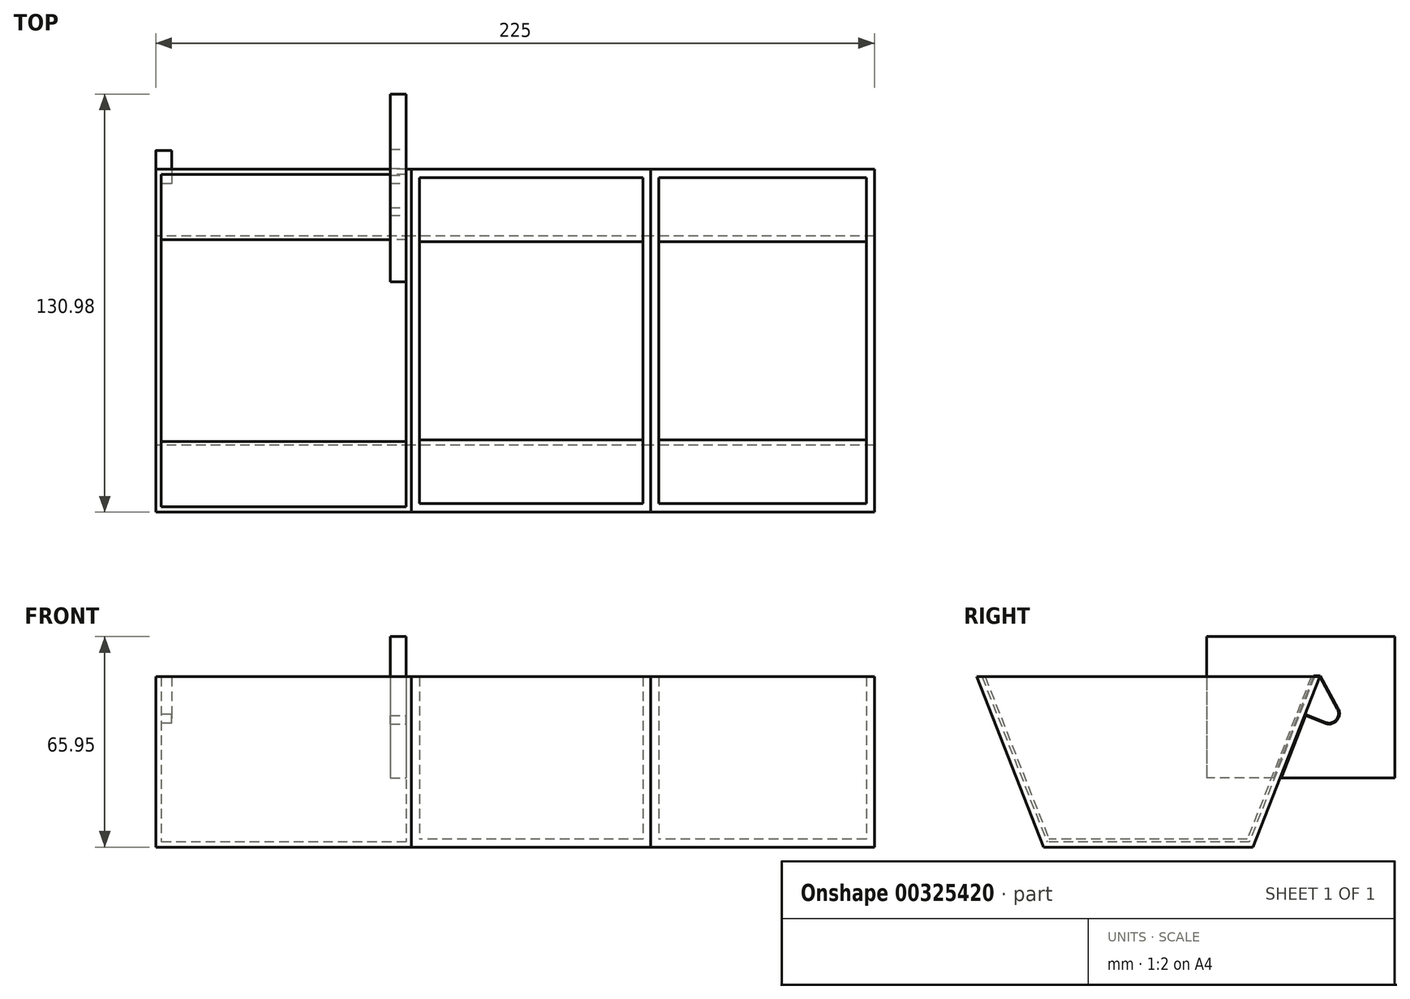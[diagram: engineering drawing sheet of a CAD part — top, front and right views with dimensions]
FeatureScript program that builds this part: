
annotation { "Feature Type Name" : "Feature", "Feature Type Description" : "" }
export const myFeature = defineFeature(function(context is Context, id is Id, definition is map)
    precondition{}
    {
        {
            var Q0;
            Q0=qCreatedBy(makeId("Right.planeOp"),FACE);
            var sketch = newSketch(context, id + "F0", { "sketchPlane" : qUnion([Q0])});
            skLineSegment(sketch, "E0", {"start": v(0, 0) * mm, "end": v(0, 53.37) * mm});
            skLineSegment(sketch, "E1", {"start": v(0, 53.37) * mm, "end": v(53.75, 53.37) * mm});
            skLineSegment(sketch, "E2", {"start": v(53.75, 53.37) * mm, "end": v(32.75, 0) * mm});
            skLineSegment(sketch, "E3", {"start": v(32.75, 0) * mm, "end": v(0, 0) * mm});
            skSolve(sketch);
        }
        {
            var Q0;
            Q0=makeQuery(id+"F0.imprint","IMPRINT",FACE,{"disambiguationData":[TD([[makeQuery(id+"F0.imprint","IMPRINT",EDGE,{"derivedFrom":sQuery(id+"F0.wireOp",EDGE,"E0")}),-1.0]])]});
            extrude(context, id + "F1", {"entities" : qUnion([Q0]), "depth" : 80 * mm});
        }
        {
            var Q0;
            Q0=makeQuery(id+"F1.opExtrude","SWEPT_BODY",BODY,{"disambiguationData":[OSD([sQuery(id+"F0.wireOp",EDGE,"E0"),sQuery(id+"F0.wireOp",EDGE,"E1"),sQuery(id+"F0.wireOp",EDGE,"E2"),sQuery(id+"F0.wireOp",EDGE,"E3")])]});
            var Q1;
            Q1=makeQuery(id+"F1.opExtrude","SWEPT_FACE",FACE,{"disambiguationData":[OSD([sQuery(id+"F0.wireOp",EDGE,"E0")])]});
            mirror(context, id + "F2", {"operationType" : NewBodyOperationType.ADD, "entities" : qUnion([Q0]), "mirrorPlane" : qUnion([Q1])});
        }
        {
            var Q0;
            {var subQ0=makeQuery(id+"F1.opExtrude","SWEPT_FACE",FACE,{"disambiguationData":[OSD([sQuery(id+"F0.wireOp",EDGE,"E1")])]});Q0=makeQuery(id+"F2.boolean.opBoolean","MERGE",FACE,{"derivedFrom":[subQ0,makeQuery(id+"F2.opPattern","COPY",FACE,{"derivedFrom":subQ0,"instanceName":"1"})]});}
            shell(context, id + "F3", {"entities" : qUnion([Q0]), "thickness" : 1.6 * mm});
        }
        {
            var Q0;
            {var subQ0=makeQuery(id+"F1.opExtrude","CAP_FACE",FACE,{"disambiguationData":[OSD([sQuery(id+"F0.wireOp",EDGE,"E0"),sQuery(id+"F0.wireOp",EDGE,"E1"),sQuery(id+"F0.wireOp",EDGE,"E2"),sQuery(id+"F0.wireOp",EDGE,"E3")])],"isStart":false});Q0=makeQuery(id+"F2.boolean.opBoolean","MERGE",FACE,{"derivedFrom":[subQ0,makeQuery(id+"F2.opPattern","COPY",FACE,{"derivedFrom":subQ0,"instanceName":"1"})]});}
            extrude(context, id + "F4", {"entities" : qUnion([Q0]), "depth" : 75 * mm});
        }
        {
            var Q0;
            Q0=makeQuery(id+"F4.opExtrude","CAP_FACE",FACE,{"disambiguationData":[OSD([sQuery(id+"F0.wireOp",EDGE,"E0"),sQuery(id+"F0.wireOp",EDGE,"E1"),sQuery(id+"F0.wireOp",EDGE,"E2"),sQuery(id+"F0.wireOp",EDGE,"E3")])],"isStart":false});
            extrude(context, id + "F5", {"entities" : qUnion([Q0]), "depth" : 70 * mm});
        }
        {
            var Q0;
            Q0=makeQuery(id+"F4.opExtrude","SWEPT_FACE",FACE,{"disambiguationData":[OSD([sQuery(id+"F0.wireOp",EDGE,"E1")])]});
            shell(context, id + "F6", {"entities" : qUnion([Q0]), "thickness" : 2.5 * mm});
        }
        {
            var Q0;
            Q0=makeQuery(id+"F5.opExtrude","SWEPT_FACE",FACE,{"disambiguationData":[OSD([sQuery(id+"F0.wireOp",EDGE,"E1")])]});
            shell(context, id + "F7", {"entities" : qUnion([Q0]), "thickness" : 2.5 * mm});
        }
        {
            var Q0;
            {var subQ0=makeQuery(id+"F1.opExtrude","CAP_FACE",FACE,{"disambiguationData":[OSD([sQuery(id+"F0.wireOp",EDGE,"E0"),sQuery(id+"F0.wireOp",EDGE,"E1"),sQuery(id+"F0.wireOp",EDGE,"E2"),sQuery(id+"F0.wireOp",EDGE,"E3")])],"isStart":true});Q0=makeQuery(id+"F2.boolean.opBoolean","MERGE",FACE,{"derivedFrom":[subQ0,makeQuery(id+"F2.opPattern","COPY",FACE,{"derivedFrom":subQ0,"instanceName":"1"})]});}
            var sketch = newSketch(context, id + "F8", { "sketchPlane" : qUnion([Q0])});
            skLineSegment(sketch, "E4", {"start": v(-53.75, 53.37) * mm, "end": v(-63.2, 36.05) * mm});
            skLineSegment(sketch, "E5", {"start": v(-63.2, 36.05) * mm, "end": v(-49.11, 41.59) * mm});
            skSolve(sketch);
        }
        {
            var Q0;
            {var subQ0=sQuery(id+"F8.wireOp",EDGE,"E4");Q0=makeQuery(id+"F8.imprint","IMPRINT",FACE,{"disambiguationData":[TD([[makeQuery(id+"F8.imprint","IMPRINT",EDGE,{"derivedFrom":subQ0}),1.0]])]});}
            extrude(context, id + "F9", {"entities" : qUnion([Q0]), "operationType" : NewBodyOperationType.ADD, "oppositeDirection" : true, "depth" : 5 * mm});
        }
        {
            var Q0;
            Q0=makeQuery(id+"F9.opExtrude","SWEPT_EDGE",EDGE,{"disambiguationData":[OSD([sQuery(id+"F8.wireOp",EDGE,"E4"),sQuery(id+"F8.wireOp",EDGE,"E5")])]});
            fillet(context, id + "F10", {"entities" : qUnion([Q0]), "radius" : 3 * mm, "tangentPropagation" : true, "allowEdgeOverflow" : false});
        }
        {
            var Q0;
            {var subQ0=sQuery(id+"F0.wireOp",EDGE,"E3");var subQ1=sQuery(id+"F0.wireOp",EDGE,"E2");var subQ2=sQuery(id+"F0.wireOp",EDGE,"E1");var subQ3=sQuery(id+"F0.wireOp",EDGE,"E0");var subQ4=makeQuery(id+"F1.opExtrude","CAP_FACE",FACE,{"disambiguationData":[OSD([subQ3,subQ2,subQ1,subQ0])],"isStart":false});Q0=makeQuery(id+"F3.opShell","OFFSET_FACE",FACE,{"disambiguationData":[OSD([subQ3,subQ2,subQ1,subQ0]),TDD([makeQuery(id+"F2.boolean.opBoolean","MERGE",FACE,{"derivedFrom":[subQ4,makeQuery(id+"F2.opPattern","COPY",FACE,{"derivedFrom":subQ4,"instanceName":"1"})]})])]});}
            var sketch = newSketch(context, id + "F11", { "sketchPlane" : qUnion([Q0])});
            skLineSegment(sketch, "E6.0", {"start": v(-49.11, 41.59) * mm, "end": v(-32.75, 0) * mm});
            skLineSegment(sketch, "E7.0", {"start": v(-55.51, 39.07) * mm, "end": v(-49.11, 41.59) * mm});
            skArc(sketch, "E8.0", {"start": v(-59.24, 43.3) * mm, "mid": v(-58.86, 39.88) * mm, "end": v(-55.51, 39.07) * mm});
            skLineSegment(sketch, "E9.0", {"start": v(-53.75, 53.37) * mm, "end": v(-59.24, 43.3) * mm});
            skLineSegment(sketch, "E10.0", {"start": v(-52.03, 53.37) * mm, "end": v(-53.75, 53.37) * mm});
            skLineSegment(sketch, "E11.0", {"start": v(-52.03, 53.37) * mm, "end": v(-31.66, 1.6) * mm});
            skPoint(sketch, "E12.orphan", {"position": v(53.75, 53.37) * mm});
            skLineSegment(sketch, "E13.0", {"start": v(-49.28, 41.2) * mm, "end": v(-41.62, 21.73) * mm});
            skLineSegment(sketch, "E13.1", {"start": v(-55.4, 38.79) * mm, "end": v(-49.28, 41.2) * mm});
            skLineSegment(sketch, "E13.2", {"start": v(-51.83, 53.67) * mm, "end": v(-39.26, 21.73) * mm});
            skLineSegment(sketch, "E13.3", {"start": v(-51.83, 53.67) * mm, "end": v(-53.93, 53.67) * mm});
            skLineSegment(sketch, "E13.4", {"start": v(-53.93, 53.67) * mm, "end": v(-59.5, 43.44) * mm});
            skArc(sketch, "E13.5", {"start": v(-59.5, 43.44) * mm, "mid": v(-59.08, 39.68) * mm, "end": v(-55.4, 38.79) * mm});
            skLineSegment(sketch, "E14.bottom", {"start": v(-77.23, 65.95) * mm, "end": v(-18.36, 65.95) * mm});
            skLineSegment(sketch, "E14.top", {"start": v(-77.23, 21.73) * mm, "end": v(-41.62, 21.73) * mm});
            skLineSegment(sketch, "E14.left", {"start": v(-77.23, 65.95) * mm, "end": v(-77.23, 21.73) * mm});
            skLineSegment(sketch, "E14.right", {"start": v(-18.36, 65.95) * mm, "end": v(-18.36, 21.73) * mm});
            skLineSegment(sketch, "E15.trimOffspring", {"start": v(-39.26, 21.73) * mm, "end": v(-18.36, 21.73) * mm});
            skSolve(sketch);
        }
        {
            var Q0;
            Q0=makeQuery(id+"F11.imprint","IMPRINT",FACE,{"disambiguationData":[TD([[makeQuery(id+"F11.imprint","IMPRINT",EDGE,{"derivedFrom":sQuery(id+"F11.wireOp",EDGE,"E13.0")}),-1.0]])]});
            var Q1;
            {var subQ0=sQuery(id+"F11.wireOp",EDGE,"E15.trimOffspring");Q1=makeQuery(id+"F11.imprint","IMPRINT",FACE,{"disambiguationData":[TD([[makeQuery(id+"F11.imprint","IMPRINT",EDGE,{"derivedFrom":subQ0}),1.0]])]});}
            extrude(context, id + "F12", {"entities" : qUnion([Q0, Q1]), "depth" : 5 * mm});
        }
    });
